# Revit family: EVC-Series
name_source: partatom
category: Lighting Fixtures
units: mm (PartAtom-declared; Revit-internal decimal feet)

## family parameters
Cut with Voids When Loaded = No
Host = Face
Light Source = Yes
OmniClass Number = 23.80.70.11
OmniClass Title = Luminaries for Internal Lighting
Part Type = Normal
Room Calculation Point = No
Round Connector Dimension = Use Diameter
Shared = Yes

## types (2) — shared parameters
Apparent Load = 0 VA
Color Filter = 16777215
Default Elevation = 48.000"
Description = The EVC Series is a compact architectural LED combination exit and emergency lighting unit designed for fast installation and reliable service
Dimming Lamp Color Temperature Shift = <None>
Glass = light Glass
Manufacturer = Dual Lighting
Model = EVC Series
Photometric Web File = generic
Tilt Angle = 0.00°
Total Input Wattage = 1-3 W
URL = https://www.currentlighting.com
Voltage = 120 V

## per-type parameters (varying)
| type | Emit from Line Length | Finish | Lens |
| EVC-W | 2.000" | White | Red Glass |
| EVC-B | 24.000" | Black | Green Glass |

## geometry (parser evidence)
native form markers: Blend x4, Sweep x5
no freeform markers — native parametric forms only
